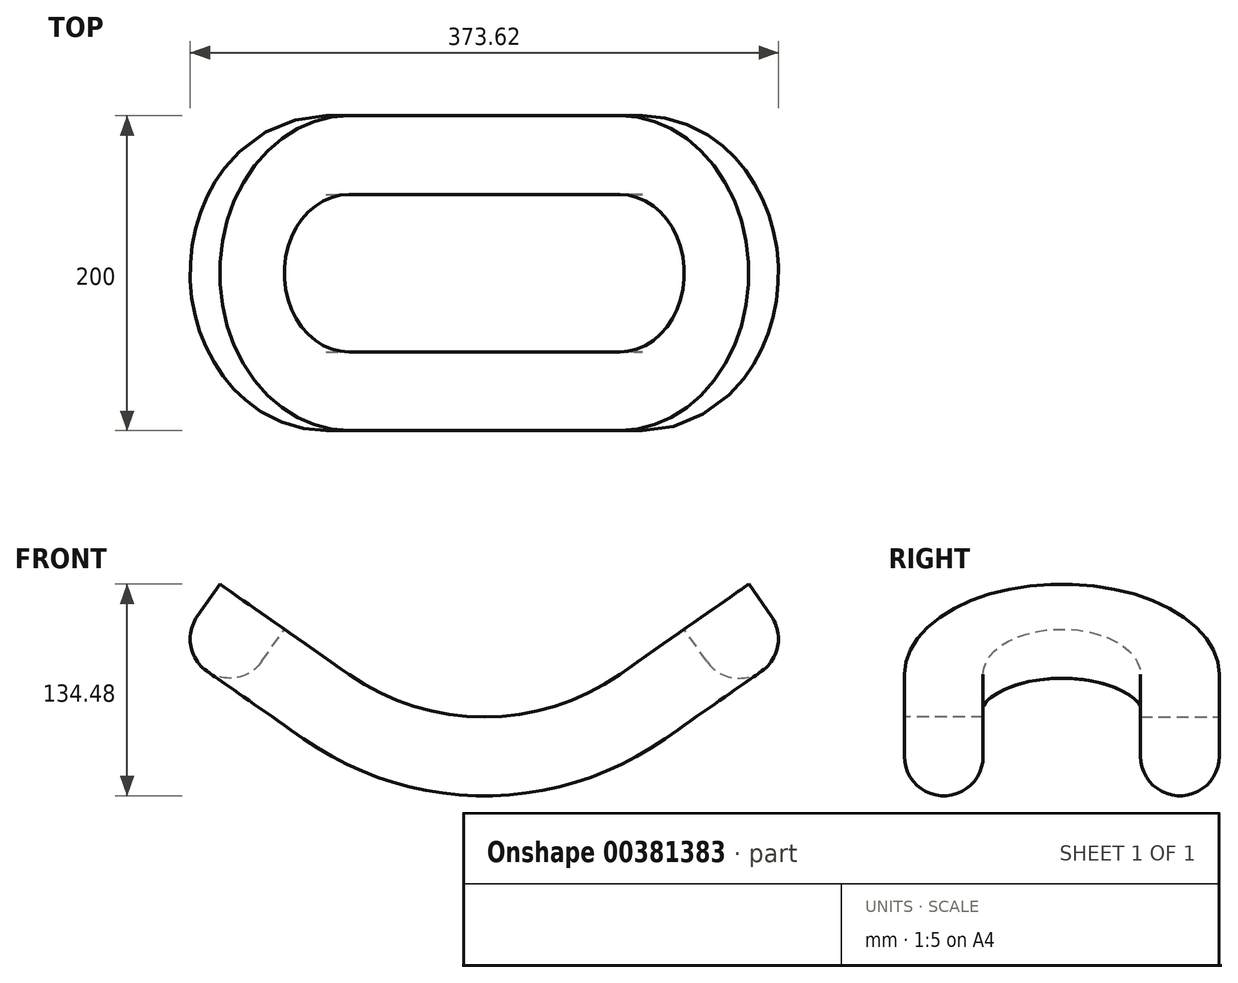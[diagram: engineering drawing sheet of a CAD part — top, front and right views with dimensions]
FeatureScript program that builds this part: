
annotation { "Feature Type Name" : "Feature", "Feature Type Description" : "" }
export const myFeature = defineFeature(function(context is Context, id is Id, definition is map)
    precondition{}
    {
        {
            var Q0;
            Q0=qCreatedBy(makeId("Front.planeOp"),FACE);
            var sketch = newSketch(context, id + "F0", { "sketchPlane" : qUnion([Q0])});
            skArc(sketch, "E0", {"start": v(0, 0) * mm, "mid": v(45.1, 6.94) * mm, "end": v(86.04, 27.13) * mm});
            skLineSegment(sketch, "E1", {"start": v(86.04, 27.13) * mm, "end": v(167.95, 84.48) * mm});
            skLineSegment(sketch, "E2", {"start": v(0, 150) * mm, "end": v(86.04, 27.13) * mm});
            skSolve(sketch);
        }
        {
            var Q0;
            Q0=sQuery(id+"F0.wireOp",EDGE,"E0");
            var Q1;
            Q1=sQuery(id+"F0.wireOp",EDGE,"E1");
            extrude(context, id + "F1", {"bodyType" : ToolBodyType.SURFACE, "surfaceEntities" : qUnion([Q0, Q1]), "depth" : 100 * mm});
        }
        {
            var Q0;
            Q0=makeQuery(id+"F1.opExtrude","SWEPT_FACE",FACE,{"disambiguationData":[OSD([sQuery(id+"F0.wireOp",EDGE,"E1")])]});
            var sketch = newSketch(context, id + "F2", { "sketchPlane" : qUnion([Q0])});
            skArc(sketch, "E3", {"start": v(186.04, 0) * mm, "mid": v(156.75, 70.71) * mm, "end": v(86.04, 100) * mm});
            skSolve(sketch);
        }
        {
            var Q0;
            Q0=qCreatedBy(makeId("Right.planeOp"),FACE);
            var sketch = newSketch(context, id + "F3", { "sketchPlane" : qUnion([Q0])});
            skLineSegment(sketch, "E4.bottom", {"start": v(-100, -25) * mm, "end": v(-50, -25) * mm, "construction": true});
            skLineSegment(sketch, "E4.top", {"start": v(-100, 0) * mm, "end": v(-50, 0) * mm});
            skLineSegment(sketch, "E4.left", {"start": v(-100, -25) * mm, "end": v(-100, 0) * mm});
            skLineSegment(sketch, "E4.right", {"start": v(-50, -25) * mm, "end": v(-50, 0) * mm});
            skArc(sketch, "E5", {"start": v(-100, -25) * mm, "mid": v(-75, -50) * mm, "end": v(-50, -25) * mm});
            skSolve(sketch);
        }
        {
            var Q0;
            Q0=makeQuery(id+"F3.imprint","IMPRINT",FACE,{"disambiguationData":[TD([[makeQuery(id+"F3.imprint","IMPRINT",EDGE,{"derivedFrom":sQuery(id+"F3.wireOp",EDGE,"E4.top")}),-1.0]])]});
            var Q1;
            Q1=makeQuery(id+"F1.opExtrude","CAP_EDGE",EDGE,{"disambiguationData":[OSD([sQuery(id+"F0.wireOp",EDGE,"E0")])],"isStart":false});
            var Q2;
            Q2=sQuery(id+"F2.wireOp",EDGE,"E3");
            sweep(context, id + "F4", {"profiles" : qUnion([Q0]), "path" : qUnion([Q1, Q2])});
        }
        {
            var Q0;
            Q0=makeQuery(id+"F4.opSweep","SWEPT_BODY",BODY,{"disambiguationData":[OSD([sQuery(id+"F2.wireOp",EDGE,"E3"),sQuery(id+"F3.wireOp",EDGE,"E4.top"),sQuery(id+"F3.wireOp",EDGE,"E4.left"),sQuery(id+"F3.wireOp",EDGE,"E4.right"),sQuery(id+"F3.wireOp",EDGE,"E5")])]});
            var Q1;
            Q1=qCreatedBy(makeId("Front.planeOp"),FACE);
            mirror(context, id + "F5", {"operationType" : NewBodyOperationType.ADD, "entities" : qUnion([Q0]), "mirrorPlane" : qUnion([Q1])});
        }
        {
            var Q0;
            Q0=makeQuery(id+"F4.opSweep","SWEPT_BODY",BODY,{"disambiguationData":[OSD([sQuery(id+"F2.wireOp",EDGE,"E3"),sQuery(id+"F3.wireOp",EDGE,"E4.top"),sQuery(id+"F3.wireOp",EDGE,"E4.left"),sQuery(id+"F3.wireOp",EDGE,"E4.right"),sQuery(id+"F3.wireOp",EDGE,"E5")])]});
            var Q1;
            Q1=qCreatedBy(makeId("Right.planeOp"),FACE);
            mirror(context, id + "F6", {"operationType" : NewBodyOperationType.ADD, "entities" : qUnion([Q0]), "mirrorPlane" : qUnion([Q1])});
        }
    });
